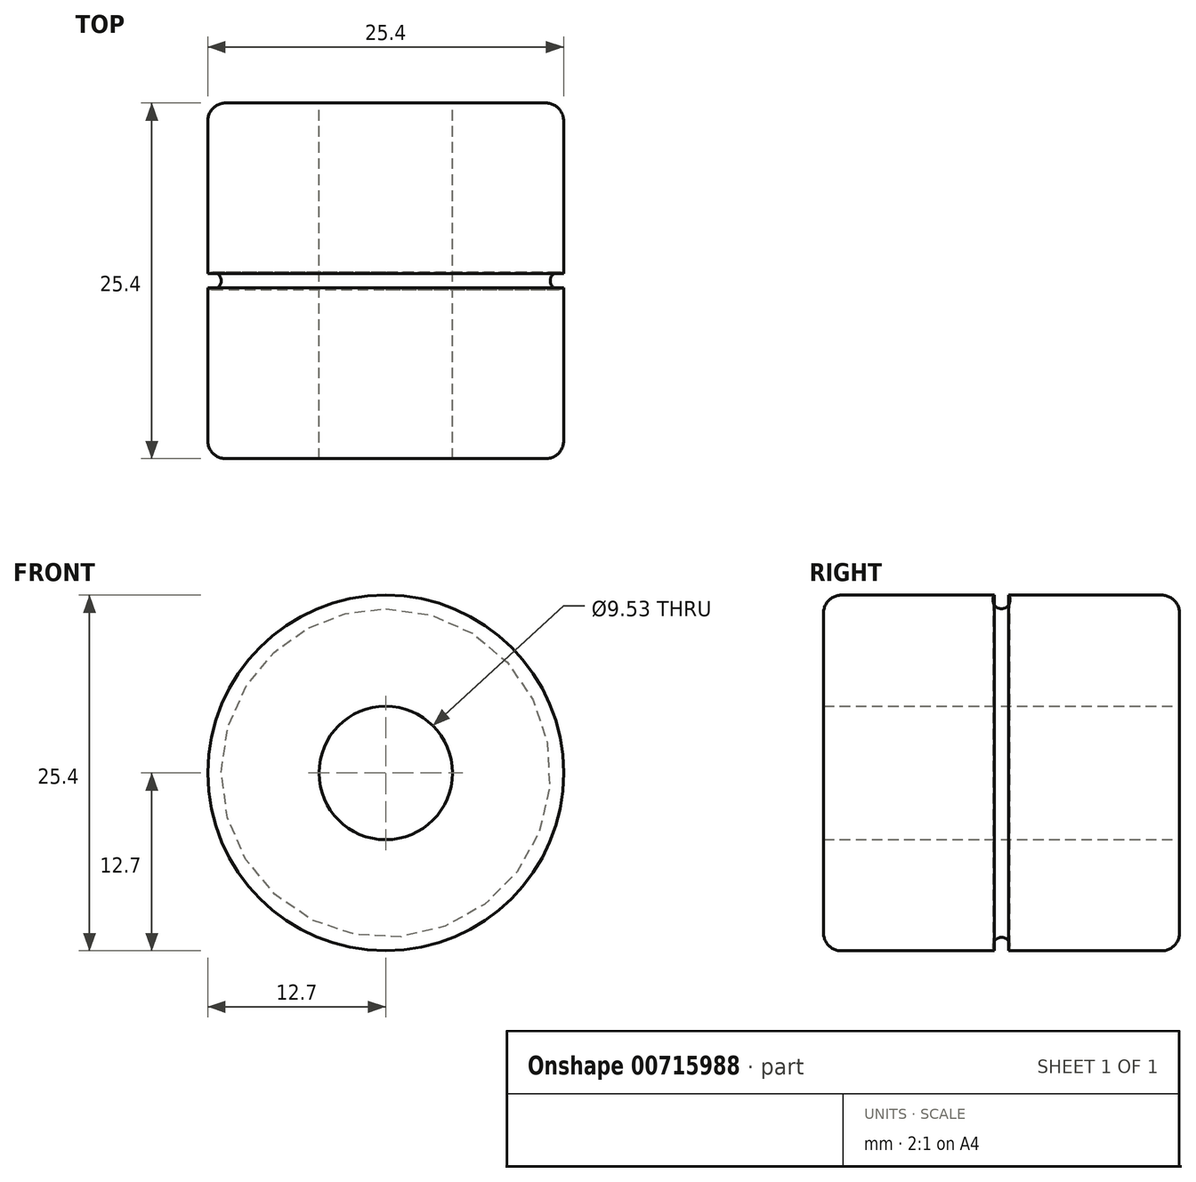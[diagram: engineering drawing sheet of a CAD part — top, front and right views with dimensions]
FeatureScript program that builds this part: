
annotation { "Feature Type Name" : "Feature", "Feature Type Description" : "" }
export const myFeature = defineFeature(function(context is Context, id is Id, definition is map)
    precondition{}
    {
        {
            var Q0;
            Q0=qCreatedBy(makeId("Front.planeOp"),FACE);
            var sketch = newSketch(context, id + "F0", { "sketchPlane" : qUnion([Q0])});
            skCircle(sketch, "E0", {"center": v(0, 0) * mm, "radius": 4.76 * mm});
            skCircle(sketch, "E1", {"center": v(0, 0) * mm, "radius": 12.7 * mm});
            skSolve(sketch);
        }
        {
            var Q0;
            Q0 = qSketchRegion(id + "F0", true);
            extrude(context, id + "F1", {"entities" : qUnion([Q0]), "depth" : 25.4 * mm, "offsetDistance" : 25.4 * mm, "symmetric" : true});
        }
        {
            var Q0;
            Q0=makeQuery(id+"F1.opExtrude","CAP_FACE",FACE,{"disambiguationData":[OSD([sQuery(id+"F0.wireOp",EDGE,"E0"),sQuery(id+"F0.wireOp",EDGE,"E1")])],"isStart":true});
            cPlane(context, id + "F2", {"entities" : qUnion([Q0]), "cplaneType" : CPlaneType.OFFSET, "offset" : 12.7 * mm, "oppositeDirection" : true, "width" : 152.4 * mm, "height" : 152.4 * mm});
        }
        {
            var Q0;
            Q0=makeQuery(id+"F1.opExtrude","CAP_EDGE",EDGE,{"disambiguationData":[OSD([sQuery(id+"F0.wireOp",EDGE,"E1")])],"isStart":true});
            var Q1;
            Q1=makeQuery(id+"F1.opExtrude","CAP_EDGE",EDGE,{"disambiguationData":[OSD([sQuery(id+"F0.wireOp",EDGE,"E1")])],"isStart":false});
            fillet(context, id + "F3", {"entities" : qUnion([Q0, Q1]), "radius" : 1.27 * mm, "tangentPropagation" : true, "allowEdgeOverflow" : false});
        }
        {
            var Q0;
            Q0=qCreatedBy(id+"F2.planeOp",FACE);
            var sketch = newSketch(context, id + "F4", { "sketchPlane" : qUnion([Q0])});
            skCircle(sketch, "E2", {"center": v(0, 0) * mm, "radius": 12.32 * mm});
            skLineSegment(sketch, "E3", {"start": v(0, 0) * mm, "end": v(0, 15.13) * mm, "construction": true});
            skLineSegment(sketch, "E4", {"start": v(0, 0) * mm, "end": v(0, -14.87) * mm, "construction": true});
            skSolve(sketch);
        }
        {
            var Q0;
            Q0=sQuery(id+"F4.wireOp",EDGE,"E3");
            cPlane(context, id + "F5", {"entities" : qUnion([Q0]), "cplaneType" : CPlaneType.LINE_ANGLE, "offset" : 25.4 * mm, "angle" : 0 * degree, "width" : 152.4 * mm, "height" : 152.4 * mm});
        }
        {
            var Q0;
            Q0=qCreatedBy(id+"F5.planeOp",FACE);
            var sketch = newSketch(context, id + "F6", { "sketchPlane" : qUnion([Q0])});
            skCircle(sketch, "E5", {"center": v(0, 12.36) * mm, "radius": 0.62 * mm});
            skSolve(sketch);
        }
        {
            var Q0;
            Q0=makeQuery(id+"F6.imprint","IMPRINT",FACE,{"disambiguationData":[TD([[makeQuery(id+"F6.imprint","IMPRINT",EDGE,{"derivedFrom":sQuery(id+"F6.wireOp",EDGE,"E5")}),1.0]])]});
            var Q1;
            Q1=sQuery(id+"F4.wireOp",EDGE,"E2");
            sweep(context, id + "F7", {"operationType" : NewBodyOperationType.REMOVE, "profiles" : qUnion([Q0]), "path" : qUnion([Q1])});
        }
    });
